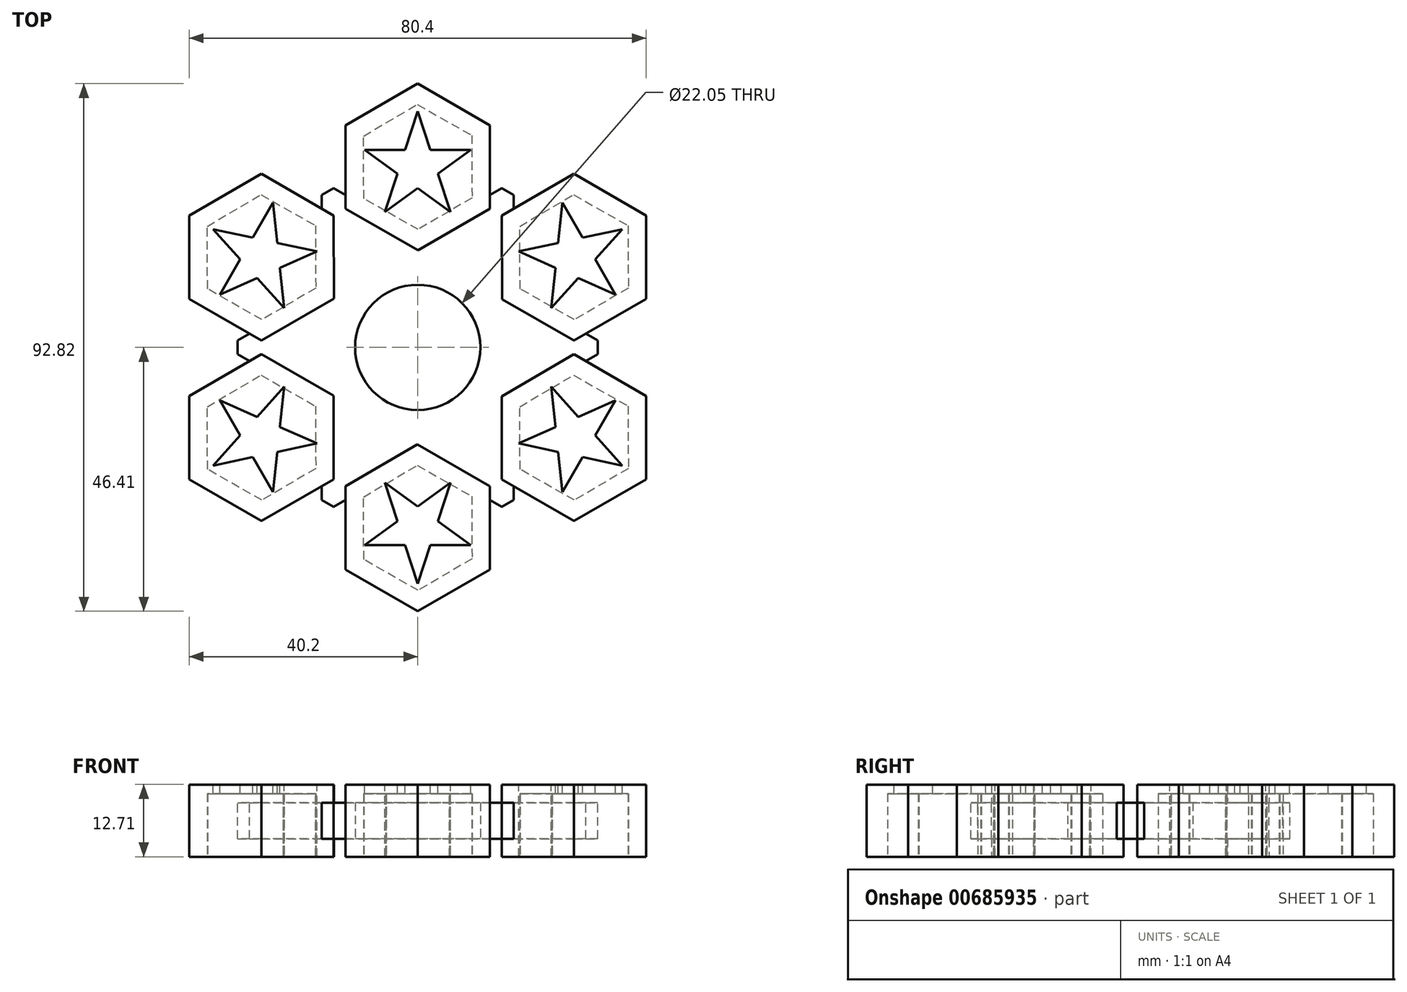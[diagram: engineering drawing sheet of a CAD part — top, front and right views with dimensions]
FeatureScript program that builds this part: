
annotation { "Feature Type Name" : "Feature", "Feature Type Description" : "" }
export const myFeature = defineFeature(function(context is Context, id is Id, definition is map)
    precondition{}
    {
        {
            var Q0;
            Q0=qCreatedBy(makeId("Top.planeOp"),FACE);
            var sketch = newSketch(context, id + "F0", { "sketchPlane" : qUnion([Q0])});
            skCircle(sketch, "E0", {"center": v(0, 0) * mm, "radius": 11.02 * mm});
            skCircle(sketch, "E1", {"center": v(0, 0) * mm, "radius": 15.88 * mm});
            skCircle(sketch, "E2.cCircle", {"center": v(0, 31.75) * mm, "radius": 9.53 * mm, "construction": true});
            skLineSegment(sketch, "E2.0", {"start": v(9.56, 26.3) * mm, "end": v(0.07, 20.75) * mm});
            skLineSegment(sketch, "E2.1", {"start": v(0.07, 20.75) * mm, "end": v(-9.5, 26.2) * mm});
            skLineSegment(sketch, "E2.2", {"start": v(-9.5, 26.2) * mm, "end": v(-9.56, 37.2) * mm});
            skLineSegment(sketch, "E2.3", {"start": v(-9.56, 37.2) * mm, "end": v(-0.07, 42.75) * mm});
            skLineSegment(sketch, "E2.4", {"start": v(-0.07, 42.75) * mm, "end": v(9.5, 37.3) * mm});
            skLineSegment(sketch, "E2.5", {"start": v(9.5, 37.3) * mm, "end": v(9.56, 26.3) * mm});
            skPoint(sketch, "E2.0.midPoint", {"position": v(4.81, 23.53) * mm});
            skLineSegment(sketch, "E3.1.0", {"start": v(-18, 21.43) * mm, "end": v(-17.94, 10.43) * mm});
            skLineSegment(sketch, "E3.1.1", {"start": v(-27.56, 26.87) * mm, "end": v(-18, 21.43) * mm});
            skLineSegment(sketch, "E3.1.2", {"start": v(-37.06, 21.32) * mm, "end": v(-27.56, 26.87) * mm});
            skLineSegment(sketch, "E3.1.3", {"start": v(-36.99, 10.32) * mm, "end": v(-37.06, 21.32) * mm});
            skLineSegment(sketch, "E3.1.4", {"start": v(-27.43, 4.88) * mm, "end": v(-36.99, 10.32) * mm});
            skLineSegment(sketch, "E3.1.5", {"start": v(-17.94, 10.43) * mm, "end": v(-27.43, 4.88) * mm});
            skCircle(sketch, "E3.1.6", {"center": v(-27.5, 15.87) * mm, "radius": 9.53 * mm, "construction": true});
            skPoint(sketch, "E3.1.7", {"position": v(-17.97, 15.93) * mm});
            skLineSegment(sketch, "E3.2.0", {"start": v(-27.56, -4.88) * mm, "end": v(-18, -10.32) * mm});
            skLineSegment(sketch, "E3.2.1", {"start": v(-37.06, -10.43) * mm, "end": v(-27.56, -4.88) * mm});
            skLineSegment(sketch, "E3.2.2", {"start": v(-36.99, -21.43) * mm, "end": v(-37.06, -10.43) * mm});
            skLineSegment(sketch, "E3.2.3", {"start": v(-27.43, -26.87) * mm, "end": v(-36.99, -21.43) * mm});
            skLineSegment(sketch, "E3.2.4", {"start": v(-17.94, -21.32) * mm, "end": v(-27.43, -26.87) * mm});
            skLineSegment(sketch, "E3.2.5", {"start": v(-18, -10.32) * mm, "end": v(-17.94, -21.32) * mm});
            skCircle(sketch, "E3.2.6", {"center": v(-27.5, -15.88) * mm, "radius": 9.53 * mm, "construction": true});
            skPoint(sketch, "E3.2.7", {"position": v(-22.79, -7.6) * mm});
            skLineSegment(sketch, "E4.2.3.0", {"start": v(-9.56, -26.3) * mm, "end": v(-0.07, -20.75) * mm});
            skLineSegment(sketch, "E4.3.3.0", {"start": v(-9.5, -37.3) * mm, "end": v(-9.56, -26.3) * mm});
            skLineSegment(sketch, "E4.6.3.0", {"start": v(0.07, -42.75) * mm, "end": v(-9.5, -37.3) * mm});
            skLineSegment(sketch, "E4.9.3.0", {"start": v(9.56, -37.2) * mm, "end": v(0.07, -42.75) * mm});
            skLineSegment(sketch, "E4.12.3.0", {"start": v(9.5, -26.2) * mm, "end": v(9.56, -37.2) * mm});
            skLineSegment(sketch, "E4.15.3.0", {"start": v(-0.07, -20.75) * mm, "end": v(9.5, -26.2) * mm});
            skCircle(sketch, "E4.18.3.0", {"center": v(0, -31.75) * mm, "radius": 9.53 * mm, "construction": true});
            skPoint(sketch, "E4.20.3.0", {"position": v(-4.81, -23.53) * mm});
            skLineSegment(sketch, "E4.2.4.0", {"start": v(18, -21.43) * mm, "end": v(17.94, -10.43) * mm});
            skLineSegment(sketch, "E4.3.4.0", {"start": v(27.56, -26.87) * mm, "end": v(18, -21.43) * mm});
            skLineSegment(sketch, "E4.6.4.0", {"start": v(37.06, -21.32) * mm, "end": v(27.56, -26.87) * mm});
            skLineSegment(sketch, "E4.9.4.0", {"start": v(36.99, -10.32) * mm, "end": v(37.06, -21.32) * mm});
            skLineSegment(sketch, "E4.12.4.0", {"start": v(27.43, -4.88) * mm, "end": v(36.99, -10.32) * mm});
            skLineSegment(sketch, "E4.15.4.0", {"start": v(17.94, -10.43) * mm, "end": v(27.43, -4.88) * mm});
            skCircle(sketch, "E4.18.4.0", {"center": v(27.5, -15.88) * mm, "radius": 9.53 * mm, "construction": true});
            skPoint(sketch, "E4.20.4.0", {"position": v(17.97, -15.93) * mm});
            skLineSegment(sketch, "E4.2.5.0", {"start": v(27.56, 4.88) * mm, "end": v(18, 10.32) * mm});
            skLineSegment(sketch, "E4.3.5.0", {"start": v(37.06, 10.43) * mm, "end": v(27.56, 4.88) * mm});
            skLineSegment(sketch, "E4.6.5.0", {"start": v(36.99, 21.43) * mm, "end": v(37.06, 10.43) * mm});
            skLineSegment(sketch, "E4.9.5.0", {"start": v(27.43, 26.87) * mm, "end": v(36.99, 21.43) * mm});
            skLineSegment(sketch, "E4.12.5.0", {"start": v(17.94, 21.32) * mm, "end": v(27.43, 26.87) * mm});
            skLineSegment(sketch, "E4.15.5.0", {"start": v(18, 10.32) * mm, "end": v(17.94, 21.32) * mm});
            skCircle(sketch, "E4.18.5.0", {"center": v(27.5, 15.87) * mm, "radius": 9.53 * mm, "construction": true});
            skPoint(sketch, "E4.20.5.0", {"position": v(22.79, 7.6) * mm});
            skCircle(sketch, "E5.cCircle", {"center": v(0, 31.75) * mm, "radius": 12.7 * mm, "construction": true});
            skLineSegment(sketch, "E5.0", {"start": v(12.7, 24.42) * mm, "end": v(0, 17.09) * mm});
            skLineSegment(sketch, "E5.1", {"start": v(0, 17.09) * mm, "end": v(-12.7, 24.42) * mm});
            skLineSegment(sketch, "E5.2", {"start": v(-12.7, 24.42) * mm, "end": v(-12.7, 39.08) * mm});
            skLineSegment(sketch, "E5.3", {"start": v(-12.7, 39.08) * mm, "end": v(0, 46.41) * mm});
            skLineSegment(sketch, "E5.4", {"start": v(0, 46.41) * mm, "end": v(12.7, 39.08) * mm});
            skLineSegment(sketch, "E5.5", {"start": v(12.7, 39.08) * mm, "end": v(12.7, 24.42) * mm});
            skPoint(sketch, "E5.0.midPoint", {"position": v(6.35, 20.75) * mm});
            skCircle(sketch, "E6.1.0", {"center": v(-27.5, 15.87) * mm, "radius": 12.7 * mm, "construction": true});
            skLineSegment(sketch, "E6.1.1", {"start": v(-40.2, 8.54) * mm, "end": v(-40.2, 23.2) * mm});
            skLineSegment(sketch, "E6.1.2", {"start": v(-40.2, 23.2) * mm, "end": v(-27.5, 30.54) * mm});
            skLineSegment(sketch, "E6.1.3", {"start": v(-14.8, 8.54) * mm, "end": v(-27.5, 1.21) * mm});
            skPoint(sketch, "E6.1.7", {"position": v(-14.8, 15.88) * mm});
            skLineSegment(sketch, "E6.1.9", {"start": v(-27.5, 30.54) * mm, "end": v(-14.8, 23.2) * mm});
            skLineSegment(sketch, "E6.1.10", {"start": v(-14.8, 23.2) * mm, "end": v(-14.8, 8.54) * mm});
            skLineSegment(sketch, "E6.1.16", {"start": v(-27.5, 1.21) * mm, "end": v(-40.2, 8.54) * mm});
            skCircle(sketch, "E6.2.0", {"center": v(-27.5, -15.88) * mm, "radius": 12.7 * mm, "construction": true});
            skLineSegment(sketch, "E6.2.1", {"start": v(-27.5, -30.54) * mm, "end": v(-40.2, -23.2) * mm});
            skLineSegment(sketch, "E6.2.2", {"start": v(-40.2, -23.2) * mm, "end": v(-40.2, -8.54) * mm});
            skLineSegment(sketch, "E6.2.3", {"start": v(-14.8, -8.54) * mm, "end": v(-14.8, -23.2) * mm});
            skPoint(sketch, "E6.2.7", {"position": v(-21.15, -4.88) * mm});
            skLineSegment(sketch, "E6.2.9", {"start": v(-40.2, -8.54) * mm, "end": v(-27.5, -1.21) * mm});
            skLineSegment(sketch, "E6.2.10", {"start": v(-27.5, -1.21) * mm, "end": v(-14.8, -8.54) * mm});
            skLineSegment(sketch, "E6.2.16", {"start": v(-14.8, -23.2) * mm, "end": v(-27.5, -30.54) * mm});
            skCircle(sketch, "E6.3.0", {"center": v(0, -31.75) * mm, "radius": 12.7 * mm, "construction": true});
            skLineSegment(sketch, "E6.3.1", {"start": v(12.7, -39.08) * mm, "end": v(0, -46.41) * mm});
            skLineSegment(sketch, "E6.3.2", {"start": v(0, -46.41) * mm, "end": v(-12.7, -39.08) * mm});
            skLineSegment(sketch, "E6.3.3", {"start": v(0, -17.09) * mm, "end": v(12.7, -24.42) * mm});
            skPoint(sketch, "E6.3.7", {"position": v(-6.35, -20.75) * mm});
            skLineSegment(sketch, "E6.3.9", {"start": v(-12.7, -39.08) * mm, "end": v(-12.7, -24.42) * mm});
            skLineSegment(sketch, "E6.3.10", {"start": v(-12.7, -24.42) * mm, "end": v(0, -17.09) * mm});
            skLineSegment(sketch, "E6.3.16", {"start": v(12.7, -24.42) * mm, "end": v(12.7, -39.08) * mm});
            skCircle(sketch, "E6.4.0", {"center": v(27.5, -15.87) * mm, "radius": 12.7 * mm, "construction": true});
            skLineSegment(sketch, "E6.4.1", {"start": v(40.2, -8.54) * mm, "end": v(40.2, -23.2) * mm});
            skLineSegment(sketch, "E6.4.2", {"start": v(40.2, -23.2) * mm, "end": v(27.5, -30.54) * mm});
            skLineSegment(sketch, "E6.4.3", {"start": v(14.8, -8.54) * mm, "end": v(27.5, -1.21) * mm});
            skPoint(sketch, "E6.4.7", {"position": v(14.8, -15.88) * mm});
            skCircle(sketch, "E6.4.8", {"center": v(27.5, -15.87) * mm, "radius": 9.53 * mm, "construction": true});
            skLineSegment(sketch, "E6.4.9", {"start": v(27.5, -30.54) * mm, "end": v(14.8, -23.2) * mm});
            skLineSegment(sketch, "E6.4.10", {"start": v(14.8, -23.2) * mm, "end": v(14.8, -8.54) * mm});
            skLineSegment(sketch, "E6.4.16", {"start": v(27.5, -1.21) * mm, "end": v(40.2, -8.54) * mm});
            skCircle(sketch, "E6.5.0", {"center": v(27.5, 15.88) * mm, "radius": 12.7 * mm, "construction": true});
            skLineSegment(sketch, "E6.5.1", {"start": v(27.5, 30.54) * mm, "end": v(40.2, 23.2) * mm});
            skLineSegment(sketch, "E6.5.2", {"start": v(40.2, 23.2) * mm, "end": v(40.2, 8.54) * mm});
            skLineSegment(sketch, "E6.5.3", {"start": v(14.8, 8.54) * mm, "end": v(14.8, 23.2) * mm});
            skPoint(sketch, "E6.5.7", {"position": v(21.15, 4.88) * mm});
            skCircle(sketch, "E6.5.8", {"center": v(27.5, 15.88) * mm, "radius": 9.53 * mm, "construction": true});
            skLineSegment(sketch, "E6.5.9", {"start": v(40.2, 8.54) * mm, "end": v(27.5, 1.21) * mm});
            skLineSegment(sketch, "E6.5.10", {"start": v(27.5, 1.21) * mm, "end": v(14.8, 8.54) * mm});
            skLineSegment(sketch, "E6.5.16", {"start": v(14.8, 23.2) * mm, "end": v(27.5, 30.54) * mm});
            skLineSegment(sketch, "E7", {"start": v(-14.8, 23.2) * mm, "end": v(-12.7, 24.42) * mm});
            skLineSegment(sketch, "E8", {"start": v(12.7, 24.42) * mm, "end": v(14.8, 23.2) * mm});
            skLineSegment(sketch, "E9", {"start": v(27.5, 1.21) * mm, "end": v(27.5, -1.21) * mm});
            skLineSegment(sketch, "E10", {"start": v(12.7, -24.42) * mm, "end": v(14.8, -23.2) * mm});
            skLineSegment(sketch, "E11", {"start": v(-14.8, -23.2) * mm, "end": v(-12.7, -24.42) * mm});
            skLineSegment(sketch, "E12", {"start": v(-27.5, 1.21) * mm, "end": v(-27.5, -1.21) * mm});
            skSolve(sketch);
        }
        {
            var Q0;
            Q0=makeQuery(id+"F0.imprint","IMPRINT",FACE,{"disambiguationData":[TD([[makeQuery(id+"F0.imprint","IMPRINT",EDGE,{"derivedFrom":sQuery(id+"F0.wireOp",EDGE,"E2.0")}),1.0]])]});
            var Q1;
            Q1=makeQuery(id+"F0.imprint","IMPRINT",FACE,{"disambiguationData":[TD([[makeQuery(id+"F0.imprint","IMPRINT",EDGE,{"derivedFrom":sQuery(id+"F0.wireOp",EDGE,"E1")}),-1.0]])]});
            var Q2;
            Q2=makeQuery(id+"F0.imprint","IMPRINT",FACE,{"disambiguationData":[TD([[makeQuery(id+"F0.imprint","IMPRINT",EDGE,{"derivedFrom":sQuery(id+"F0.wireOp",EDGE,"E6.1.1")}),-1.0]])]});
            var Q3;
            Q3=makeQuery(id+"F0.imprint","IMPRINT",FACE,{"disambiguationData":[TD([[makeQuery(id+"F0.imprint","IMPRINT",EDGE,{"derivedFrom":sQuery(id+"F0.wireOp",EDGE,"E6.2.1")}),-1.0]])]});
            var Q4;
            Q4=makeQuery(id+"F0.imprint","IMPRINT",FACE,{"disambiguationData":[TD([[makeQuery(id+"F0.imprint","IMPRINT",EDGE,{"derivedFrom":sQuery(id+"F0.wireOp",EDGE,"E6.3.1")}),-1.0]])]});
            var Q5;
            Q5=makeQuery(id+"F0.imprint","IMPRINT",FACE,{"disambiguationData":[TD([[makeQuery(id+"F0.imprint","IMPRINT",EDGE,{"derivedFrom":sQuery(id+"F0.wireOp",EDGE,"E6.4.1")}),-1.0]])]});
            var Q6;
            Q6=makeQuery(id+"F0.imprint","IMPRINT",FACE,{"disambiguationData":[TD([[makeQuery(id+"F0.imprint","IMPRINT",EDGE,{"derivedFrom":sQuery(id+"F0.wireOp",EDGE,"E6.5.1")}),-1.0]])]});
            var Q7;
            Q7=makeQuery(id+"F0.imprint","IMPRINT",FACE,{"disambiguationData":[TD([[makeQuery(id+"F0.imprint","IMPRINT",EDGE,{"derivedFrom":sQuery(id+"F0.wireOp",EDGE,"E0")}),-1.0]])]});
            extrude(context, id + "F1", {"entities" : qUnion([Q0, Q1, Q2, Q3, Q4, Q5, Q6, Q7]), "depth" : 6.35 * mm, "offsetDistance" : 25.4 * mm});
        }
        {
            var Q0;
            Q0=makeQuery(id+"F1.opExtrude","CAP_FACE",FACE,{"disambiguationData":[OSD([sQuery(id+"F0.wireOp",EDGE,"E1"),sQuery(id+"F0.wireOp",EDGE,"E2.0"),sQuery(id+"F0.wireOp",EDGE,"E2.1"),sQuery(id+"F0.wireOp",EDGE,"E2.2"),sQuery(id+"F0.wireOp",EDGE,"E2.3"),sQuery(id+"F0.wireOp",EDGE,"E2.4"),sQuery(id+"F0.wireOp",EDGE,"E5.2"),sQuery(id+"F0.wireOp",EDGE,"E5.3"),sQuery(id+"F0.wireOp",EDGE,"E5.4"),sQuery(id+"F0.wireOp",EDGE,"E5.5"),sQuery(id+"F0.wireOp",EDGE,"E6.1.1"),sQuery(id+"F0.wireOp",EDGE,"E6.1.2"),sQuery(id+"F0.wireOp",EDGE,"E3.1.1"),sQuery(id+"F0.wireOp",EDGE,"E6.1.9"),sQuery(id+"F0.wireOp",EDGE,"E3.1.2"),sQuery(id+"F0.wireOp",EDGE,"E3.1.3"),sQuery(id+"F0.wireOp",EDGE,"E3.1.4"),sQuery(id+"F0.wireOp",EDGE,"E3.1.5"),sQuery(id+"F0.wireOp",EDGE,"E3.1.0"),sQuery(id+"F0.wireOp",EDGE,"E6.1.16"),sQuery(id+"F0.wireOp",EDGE,"E6.2.1"),sQuery(id+"F0.wireOp",EDGE,"E6.2.2"),sQuery(id+"F0.wireOp",EDGE,"E3.2.1"),sQuery(id+"F0.wireOp",EDGE,"E6.2.9"),sQuery(id+"F0.wireOp",EDGE,"E3.2.2"),sQuery(id+"F0.wireOp",EDGE,"E3.2.3"),sQuery(id+"F0.wireOp",EDGE,"E3.2.4"),sQuery(id+"F0.wireOp",EDGE,"E3.2.5"),sQuery(id+"F0.wireOp",EDGE,"E3.2.0"),sQuery(id+"F0.wireOp",EDGE,"E6.2.16"),sQuery(id+"F0.wireOp",EDGE,"E6.3.1"),sQuery(id+"F0.wireOp",EDGE,"E6.3.2"),sQuery(id+"F0.wireOp",EDGE,"E4.3.3.0"),sQuery(id+"F0.wireOp",EDGE,"E6.3.9"),sQuery(id+"F0.wireOp",EDGE,"E4.6.3.0"),sQuery(id+"F0.wireOp",EDGE,"E4.9.3.0"),sQuery(id+"F0.wireOp",EDGE,"E4.12.3.0"),sQuery(id+"F0.wireOp",EDGE,"E4.15.3.0"),sQuery(id+"F0.wireOp",EDGE,"E4.2.3.0"),sQuery(id+"F0.wireOp",EDGE,"E6.3.16"),sQuery(id+"F0.wireOp",EDGE,"E6.4.1"),sQuery(id+"F0.wireOp",EDGE,"E6.4.2"),sQuery(id+"F0.wireOp",EDGE,"E4.3.4.0"),sQuery(id+"F0.wireOp",EDGE,"E6.4.9"),sQuery(id+"F0.wireOp",EDGE,"E4.6.4.0"),sQuery(id+"F0.wireOp",EDGE,"E4.9.4.0"),sQuery(id+"F0.wireOp",EDGE,"E4.12.4.0"),sQuery(id+"F0.wireOp",EDGE,"E4.15.4.0"),sQuery(id+"F0.wireOp",EDGE,"E4.2.4.0"),sQuery(id+"F0.wireOp",EDGE,"E6.4.16"),sQuery(id+"F0.wireOp",EDGE,"E6.5.1"),sQuery(id+"F0.wireOp",EDGE,"E6.5.2"),sQuery(id+"F0.wireOp",EDGE,"E2.5"),sQuery(id+"F0.wireOp",EDGE,"E4.3.5.0"),sQuery(id+"F0.wireOp",EDGE,"E6.5.9"),sQuery(id+"F0.wireOp",EDGE,"E4.6.5.0"),sQuery(id+"F0.wireOp",EDGE,"E4.9.5.0"),sQuery(id+"F0.wireOp",EDGE,"E4.12.5.0"),sQuery(id+"F0.wireOp",EDGE,"E4.15.5.0"),sQuery(id+"F0.wireOp",EDGE,"E4.2.5.0"),sQuery(id+"F0.wireOp",EDGE,"E6.5.16"),sQuery(id+"F0.wireOp",EDGE,"E7"),sQuery(id+"F0.wireOp",EDGE,"E8"),sQuery(id+"F0.wireOp",EDGE,"E9"),sQuery(id+"F0.wireOp",EDGE,"E10"),sQuery(id+"F0.wireOp",EDGE,"E11"),sQuery(id+"F0.wireOp",EDGE,"E12")])],"isStart":false});
            var sketch = newSketch(context, id + "F2", { "sketchPlane" : qUnion([Q0])});
            skLineSegment(sketch, "E13.0", {"start": v(0, 46.41) * mm, "end": v(12.7, 39.08) * mm});
            skPoint(sketch, "E14.0", {"position": v(-6.35, 42.75) * mm});
            skLineSegment(sketch, "E15.0", {"start": v(-12.7, 39.08) * mm, "end": v(0, 46.41) * mm});
            skLineSegment(sketch, "E16.0", {"start": v(-12.7, 24.42) * mm, "end": v(-12.7, 39.08) * mm});
            skLineSegment(sketch, "E17.0", {"start": v(12.7, 39.08) * mm, "end": v(12.7, 24.42) * mm});
            skLineSegment(sketch, "E18", {"start": v(-12.7, 24.42) * mm, "end": v(0.07, 17.08) * mm});
            skLineSegment(sketch, "E19", {"start": v(0.07, 17.08) * mm, "end": v(12.7, 24.42) * mm});
            skLineSegment(sketch, "E20.0", {"start": v(-9.56, 37.2) * mm, "end": v(-0.07, 42.75) * mm});
            skLineSegment(sketch, "E21.0", {"start": v(-9.5, 26.2) * mm, "end": v(-9.56, 37.2) * mm});
            skLineSegment(sketch, "E22.0", {"start": v(0.07, 20.75) * mm, "end": v(-9.5, 26.2) * mm});
            skLineSegment(sketch, "E23.0", {"start": v(9.56, 26.3) * mm, "end": v(0.07, 20.75) * mm});
            skLineSegment(sketch, "E24.0", {"start": v(9.5, 37.3) * mm, "end": v(9.56, 26.3) * mm});
            skLineSegment(sketch, "E25.0", {"start": v(-0.07, 42.75) * mm, "end": v(9.5, 37.3) * mm});
            skLineSegment(sketch, "E26.1.0", {"start": v(-40.2, 8.54) * mm, "end": v(-40.2, 23.2) * mm});
            skLineSegment(sketch, "E26.1.1", {"start": v(-27.5, 1.21) * mm, "end": v(-40.2, 8.54) * mm});
            skLineSegment(sketch, "E26.1.2", {"start": v(-27.5, 1.21) * mm, "end": v(-14.76, 8.6) * mm});
            skLineSegment(sketch, "E26.1.3", {"start": v(-14.76, 8.6) * mm, "end": v(-14.8, 23.2) * mm});
            skLineSegment(sketch, "E26.1.4", {"start": v(-27.5, 30.54) * mm, "end": v(-14.8, 23.2) * mm});
            skLineSegment(sketch, "E26.1.5", {"start": v(-40.2, 23.2) * mm, "end": v(-27.5, 30.54) * mm});
            skLineSegment(sketch, "E26.1.6", {"start": v(-37.06, 21.32) * mm, "end": v(-27.56, 26.87) * mm});
            skLineSegment(sketch, "E26.1.7", {"start": v(-36.99, 10.32) * mm, "end": v(-37.06, 21.32) * mm});
            skLineSegment(sketch, "E26.1.8", {"start": v(-27.43, 4.88) * mm, "end": v(-36.99, 10.32) * mm});
            skLineSegment(sketch, "E26.1.9", {"start": v(-17.94, 10.43) * mm, "end": v(-27.43, 4.88) * mm});
            skLineSegment(sketch, "E26.1.10", {"start": v(-18, 21.43) * mm, "end": v(-17.94, 10.43) * mm});
            skLineSegment(sketch, "E26.1.11", {"start": v(-27.56, 26.87) * mm, "end": v(-18, 21.43) * mm});
            skLineSegment(sketch, "E26.2.0", {"start": v(-27.5, -30.54) * mm, "end": v(-40.2, -23.2) * mm});
            skLineSegment(sketch, "E26.2.1", {"start": v(-14.8, -23.2) * mm, "end": v(-27.5, -30.54) * mm});
            skLineSegment(sketch, "E26.2.2", {"start": v(-14.8, -23.2) * mm, "end": v(-14.83, -8.48) * mm});
            skLineSegment(sketch, "E26.2.3", {"start": v(-14.83, -8.48) * mm, "end": v(-27.5, -1.21) * mm});
            skLineSegment(sketch, "E26.2.4", {"start": v(-40.2, -8.54) * mm, "end": v(-27.5, -1.21) * mm});
            skLineSegment(sketch, "E26.2.5", {"start": v(-40.2, -23.2) * mm, "end": v(-40.2, -8.54) * mm});
            skLineSegment(sketch, "E26.2.6", {"start": v(-36.99, -21.43) * mm, "end": v(-37.06, -10.43) * mm});
            skLineSegment(sketch, "E26.2.7", {"start": v(-27.43, -26.87) * mm, "end": v(-36.99, -21.43) * mm});
            skLineSegment(sketch, "E26.2.8", {"start": v(-17.94, -21.32) * mm, "end": v(-27.43, -26.87) * mm});
            skLineSegment(sketch, "E26.2.9", {"start": v(-18, -10.32) * mm, "end": v(-17.94, -21.32) * mm});
            skLineSegment(sketch, "E26.2.10", {"start": v(-27.56, -4.88) * mm, "end": v(-18, -10.32) * mm});
            skLineSegment(sketch, "E26.2.11", {"start": v(-37.06, -10.43) * mm, "end": v(-27.56, -4.88) * mm});
            skPoint(sketch, "E26.center", {"position": v(0, 0) * mm});
            skLineSegment(sketch, "E27.1.3.0", {"start": v(12.7, -39.08) * mm, "end": v(0, -46.41) * mm});
            skLineSegment(sketch, "E27.3.3.0", {"start": v(12.7, -24.42) * mm, "end": v(12.7, -39.08) * mm});
            skLineSegment(sketch, "E27.6.3.0", {"start": v(12.7, -24.42) * mm, "end": v(-0.07, -17.08) * mm});
            skLineSegment(sketch, "E27.9.3.0", {"start": v(-0.07, -17.08) * mm, "end": v(-12.7, -24.42) * mm});
            skLineSegment(sketch, "E27.12.3.0", {"start": v(-12.7, -39.08) * mm, "end": v(-12.7, -24.42) * mm});
            skLineSegment(sketch, "E27.15.3.0", {"start": v(0, -46.41) * mm, "end": v(-12.7, -39.08) * mm});
            skLineSegment(sketch, "E27.18.3.0", {"start": v(0.07, -42.75) * mm, "end": v(-9.5, -37.3) * mm});
            skLineSegment(sketch, "E27.21.3.0", {"start": v(9.56, -37.2) * mm, "end": v(0.07, -42.75) * mm});
            skLineSegment(sketch, "E27.24.3.0", {"start": v(9.5, -26.2) * mm, "end": v(9.56, -37.2) * mm});
            skLineSegment(sketch, "E27.27.3.0", {"start": v(-0.07, -20.75) * mm, "end": v(9.5, -26.2) * mm});
            skLineSegment(sketch, "E27.30.3.0", {"start": v(-9.56, -26.3) * mm, "end": v(-0.07, -20.75) * mm});
            skLineSegment(sketch, "E27.33.3.0", {"start": v(-9.5, -37.3) * mm, "end": v(-9.56, -26.3) * mm});
            skLineSegment(sketch, "E27.1.4.0", {"start": v(40.2, -8.54) * mm, "end": v(40.2, -23.2) * mm});
            skLineSegment(sketch, "E27.3.4.0", {"start": v(27.5, -1.21) * mm, "end": v(40.2, -8.54) * mm});
            skLineSegment(sketch, "E27.6.4.0", {"start": v(27.5, -1.21) * mm, "end": v(14.76, -8.6) * mm});
            skLineSegment(sketch, "E27.9.4.0", {"start": v(14.76, -8.6) * mm, "end": v(14.8, -23.2) * mm});
            skLineSegment(sketch, "E27.12.4.0", {"start": v(27.5, -30.54) * mm, "end": v(14.8, -23.2) * mm});
            skLineSegment(sketch, "E27.15.4.0", {"start": v(40.2, -23.2) * mm, "end": v(27.5, -30.54) * mm});
            skLineSegment(sketch, "E27.18.4.0", {"start": v(37.06, -21.32) * mm, "end": v(27.56, -26.87) * mm});
            skLineSegment(sketch, "E27.21.4.0", {"start": v(36.99, -10.32) * mm, "end": v(37.06, -21.32) * mm});
            skLineSegment(sketch, "E27.24.4.0", {"start": v(27.43, -4.88) * mm, "end": v(36.99, -10.32) * mm});
            skLineSegment(sketch, "E27.27.4.0", {"start": v(17.94, -10.43) * mm, "end": v(27.43, -4.88) * mm});
            skLineSegment(sketch, "E27.30.4.0", {"start": v(18, -21.43) * mm, "end": v(17.94, -10.43) * mm});
            skLineSegment(sketch, "E27.33.4.0", {"start": v(27.56, -26.87) * mm, "end": v(18, -21.43) * mm});
            skLineSegment(sketch, "E27.1.5.0", {"start": v(27.5, 30.54) * mm, "end": v(40.2, 23.2) * mm});
            skLineSegment(sketch, "E27.3.5.0", {"start": v(14.8, 23.2) * mm, "end": v(27.5, 30.54) * mm});
            skLineSegment(sketch, "E27.6.5.0", {"start": v(14.8, 23.2) * mm, "end": v(14.83, 8.48) * mm});
            skLineSegment(sketch, "E27.9.5.0", {"start": v(14.83, 8.48) * mm, "end": v(27.5, 1.21) * mm});
            skLineSegment(sketch, "E27.12.5.0", {"start": v(40.2, 8.54) * mm, "end": v(27.5, 1.21) * mm});
            skLineSegment(sketch, "E27.15.5.0", {"start": v(40.2, 23.2) * mm, "end": v(40.2, 8.54) * mm});
            skLineSegment(sketch, "E27.18.5.0", {"start": v(36.99, 21.43) * mm, "end": v(37.06, 10.43) * mm});
            skLineSegment(sketch, "E27.21.5.0", {"start": v(27.43, 26.87) * mm, "end": v(36.99, 21.43) * mm});
            skLineSegment(sketch, "E27.24.5.0", {"start": v(17.94, 21.32) * mm, "end": v(27.43, 26.87) * mm});
            skLineSegment(sketch, "E27.27.5.0", {"start": v(18, 10.32) * mm, "end": v(17.94, 21.32) * mm});
            skLineSegment(sketch, "E27.30.5.0", {"start": v(27.56, 4.88) * mm, "end": v(18, 10.32) * mm});
            skLineSegment(sketch, "E27.33.5.0", {"start": v(37.06, 10.43) * mm, "end": v(27.56, 4.88) * mm});
            skSolve(sketch);
        }
        {
            var Q0;
            Q0=makeQuery(id+"F2.imprint","IMPRINT",FACE,{"disambiguationData":[TD([[makeQuery(id+"F2.imprint","IMPRINT",EDGE,{"derivedFrom":sQuery(id+"F2.wireOp",EDGE,"E13.0")}),-1.0]])]});
            var Q1;
            Q1=makeQuery(id+"F2.imprint","IMPRINT",FACE,{"disambiguationData":[TD([[makeQuery(id+"F2.imprint","IMPRINT",EDGE,{"derivedFrom":sQuery(id+"F2.wireOp",EDGE,"E27.1.5.0")}),-1.0]])]});
            var Q2;
            Q2=makeQuery(id+"F2.imprint","IMPRINT",FACE,{"disambiguationData":[TD([[makeQuery(id+"F2.imprint","IMPRINT",EDGE,{"derivedFrom":sQuery(id+"F2.wireOp",EDGE,"E27.1.4.0")}),-1.0]])]});
            var Q3;
            Q3=makeQuery(id+"F2.imprint","IMPRINT",FACE,{"disambiguationData":[TD([[makeQuery(id+"F2.imprint","IMPRINT",EDGE,{"derivedFrom":sQuery(id+"F2.wireOp",EDGE,"E27.1.3.0")}),-1.0]])]});
            var Q4;
            Q4=makeQuery(id+"F2.imprint","IMPRINT",FACE,{"disambiguationData":[TD([[makeQuery(id+"F2.imprint","IMPRINT",EDGE,{"derivedFrom":sQuery(id+"F2.wireOp",EDGE,"E26.2.0")}),-1.0]])]});
            var Q5;
            Q5=makeQuery(id+"F2.imprint","IMPRINT",FACE,{"disambiguationData":[TD([[makeQuery(id+"F2.imprint","IMPRINT",EDGE,{"derivedFrom":sQuery(id+"F2.wireOp",EDGE,"E26.1.0")}),-1.0]])]});
            extrude(context, id + "F3", {"entities" : qUnion([Q0, Q1, Q2, Q3, Q4, Q5]), "operationType" : NewBodyOperationType.ADD, "depth" : 1.59 * mm, "offsetDistance" : 25.4 * mm, "hasSecondDirection" : true, "secondDirectionOppositeDirection" : true, "secondDirectionDepth" : 9.52 * mm});
        }
        {
            var Q0;
            Q0=makeQuery(id+"F3.opExtrude","CAP_FACE",FACE,{"disambiguationData":[OSD([sQuery(id+"F2.wireOp",EDGE,"E13.0"),sQuery(id+"F2.wireOp",EDGE,"E15.0"),sQuery(id+"F2.wireOp",EDGE,"E16.0"),sQuery(id+"F2.wireOp",EDGE,"E17.0"),sQuery(id+"F2.wireOp",EDGE,"E18"),sQuery(id+"F2.wireOp",EDGE,"E19"),sQuery(id+"F2.wireOp",EDGE,"E20.0"),sQuery(id+"F2.wireOp",EDGE,"E21.0"),sQuery(id+"F2.wireOp",EDGE,"E22.0"),sQuery(id+"F2.wireOp",EDGE,"E23.0"),sQuery(id+"F2.wireOp",EDGE,"E24.0"),sQuery(id+"F2.wireOp",EDGE,"E25.0")])],"isStart":false});
            var sketch = newSketch(context, id + "F4", { "sketchPlane" : qUnion([Q0])});
            skLineSegment(sketch, "E28.0", {"start": v(-12.7, 39.08) * mm, "end": v(0, 46.41) * mm});
            skLineSegment(sketch, "E29.0", {"start": v(-12.7, 24.42) * mm, "end": v(-12.7, 39.08) * mm});
            skLineSegment(sketch, "E30.0", {"start": v(-12.7, 24.42) * mm, "end": v(0.07, 17.08) * mm});
            skLineSegment(sketch, "E31.0", {"start": v(0.07, 17.08) * mm, "end": v(12.7, 24.42) * mm});
            skLineSegment(sketch, "E32.0", {"start": v(12.7, 39.08) * mm, "end": v(12.7, 24.42) * mm});
            skLineSegment(sketch, "E33.0", {"start": v(0, 46.41) * mm, "end": v(12.7, 39.08) * mm});
            skLineSegment(sketch, "E34.0", {"start": v(14.8, 23.2) * mm, "end": v(27.5, 30.54) * mm});
            skLineSegment(sketch, "E35.0", {"start": v(27.5, 30.54) * mm, "end": v(40.2, 23.2) * mm});
            skLineSegment(sketch, "E36.0", {"start": v(40.2, 23.2) * mm, "end": v(40.2, 8.54) * mm});
            skLineSegment(sketch, "E37.0", {"start": v(40.2, 8.54) * mm, "end": v(27.5, 1.21) * mm});
            skLineSegment(sketch, "E38.0", {"start": v(14.83, 8.48) * mm, "end": v(27.5, 1.21) * mm});
            skLineSegment(sketch, "E39.0", {"start": v(14.8, 23.2) * mm, "end": v(14.83, 8.48) * mm});
            skLineSegment(sketch, "E40.0", {"start": v(27.5, -1.21) * mm, "end": v(14.76, -8.6) * mm});
            skLineSegment(sketch, "E41.0", {"start": v(27.5, -1.21) * mm, "end": v(40.2, -8.54) * mm});
            skLineSegment(sketch, "E42.0", {"start": v(40.2, -8.54) * mm, "end": v(40.2, -23.2) * mm});
            skLineSegment(sketch, "E43.0", {"start": v(40.2, -23.2) * mm, "end": v(27.5, -30.54) * mm});
            skLineSegment(sketch, "E44.0", {"start": v(27.5, -30.54) * mm, "end": v(14.8, -23.2) * mm});
            skLineSegment(sketch, "E45.0", {"start": v(14.76, -8.6) * mm, "end": v(14.8, -23.2) * mm});
            skLineSegment(sketch, "E46.0", {"start": v(12.7, -24.42) * mm, "end": v(-0.07, -17.08) * mm});
            skLineSegment(sketch, "E47.0", {"start": v(12.7, -24.42) * mm, "end": v(12.7, -39.08) * mm});
            skLineSegment(sketch, "E48.0", {"start": v(12.7, -39.08) * mm, "end": v(0, -46.41) * mm});
            skLineSegment(sketch, "E49.0", {"start": v(0, -46.41) * mm, "end": v(-12.7, -39.08) * mm});
            skLineSegment(sketch, "E50.0", {"start": v(-12.7, -39.08) * mm, "end": v(-12.7, -24.42) * mm});
            skLineSegment(sketch, "E51.0", {"start": v(-0.07, -17.08) * mm, "end": v(-12.7, -24.42) * mm});
            skLineSegment(sketch, "E52.0", {"start": v(-14.8, -23.2) * mm, "end": v(-14.83, -8.48) * mm});
            skLineSegment(sketch, "E53.0", {"start": v(-14.8, -23.2) * mm, "end": v(-27.5, -30.54) * mm});
            skLineSegment(sketch, "E54.0", {"start": v(-27.5, -30.54) * mm, "end": v(-40.2, -23.2) * mm});
            skLineSegment(sketch, "E55.0", {"start": v(-40.2, -23.2) * mm, "end": v(-40.2, -8.54) * mm});
            skLineSegment(sketch, "E56.0", {"start": v(-40.2, -8.54) * mm, "end": v(-27.5, -1.21) * mm});
            skLineSegment(sketch, "E57.0", {"start": v(-14.83, -8.48) * mm, "end": v(-27.5, -1.21) * mm});
            skLineSegment(sketch, "E58.0", {"start": v(-27.5, 1.21) * mm, "end": v(-14.76, 8.6) * mm});
            skLineSegment(sketch, "E59.0", {"start": v(-27.5, 1.21) * mm, "end": v(-40.2, 8.54) * mm});
            skLineSegment(sketch, "E60.0", {"start": v(-40.2, 8.54) * mm, "end": v(-40.2, 23.2) * mm});
            skLineSegment(sketch, "E61.0", {"start": v(-40.2, 23.2) * mm, "end": v(-27.5, 30.54) * mm});
            skLineSegment(sketch, "E62.0", {"start": v(-27.5, 30.54) * mm, "end": v(-14.8, 23.2) * mm});
            skLineSegment(sketch, "E63.0", {"start": v(-14.76, 8.6) * mm, "end": v(-14.8, 23.2) * mm});
            skSolve(sketch);
        }
        {
            var Q0;
            Q0=makeQuery(id+"F4.imprint","IMPRINT",FACE,{"disambiguationData":[TD([[makeQuery(id+"F4.imprint","IMPRINT",EDGE,{"derivedFrom":sQuery(id+"F4.wireOp",EDGE,"E28.0")}),-1.0]])]});
            var Q1;
            Q1=makeQuery(id+"F4.imprint","IMPRINT",FACE,{"disambiguationData":[TD([[makeQuery(id+"F4.imprint","IMPRINT",EDGE,{"derivedFrom":makeQuery(id+"F3.opExtrude","CAP_EDGE",EDGE,{"disambiguationData":[OSD([sQuery(id+"F2.wireOp",EDGE,"E20.0")])],"isStart":false})}),-1.0]])]});
            var Q2;
            Q2=makeQuery(id+"F4.imprint","IMPRINT",FACE,{"disambiguationData":[TD([[makeQuery(id+"F4.imprint","IMPRINT",EDGE,{"derivedFrom":sQuery(id+"F4.wireOp",EDGE,"E34.0")}),-1.0]])]});
            var Q3;
            Q3=makeQuery(id+"F4.imprint","IMPRINT",FACE,{"disambiguationData":[TD([[makeQuery(id+"F4.imprint","IMPRINT",EDGE,{"derivedFrom":sQuery(id+"F4.wireOp",EDGE,"E40.0")}),1.0]])]});
            var Q4;
            Q4=makeQuery(id+"F4.imprint","IMPRINT",FACE,{"disambiguationData":[TD([[makeQuery(id+"F4.imprint","IMPRINT",EDGE,{"derivedFrom":sQuery(id+"F4.wireOp",EDGE,"E46.0")}),1.0]])]});
            var Q5;
            Q5=makeQuery(id+"F4.imprint","IMPRINT",FACE,{"disambiguationData":[TD([[makeQuery(id+"F4.imprint","IMPRINT",EDGE,{"derivedFrom":sQuery(id+"F4.wireOp",EDGE,"E52.0")}),1.0]])]});
            var Q6;
            Q6=makeQuery(id+"F4.imprint","IMPRINT",FACE,{"disambiguationData":[TD([[makeQuery(id+"F4.imprint","IMPRINT",EDGE,{"derivedFrom":sQuery(id+"F4.wireOp",EDGE,"E58.0")}),1.0]])]});
            extrude(context, id + "F5", {"entities" : qUnion([Q0, Q1, Q2, Q3, Q4, Q5, Q6]), "operationType" : NewBodyOperationType.ADD, "depth" : 1.59 * mm, "offsetDistance" : 25.4 * mm});
        }
        {
            var Q0;
            Q0=makeQuery(id+"F5.opExtrude","CAP_FACE",FACE,{"disambiguationData":[OSD([sQuery(id+"F4.wireOp",EDGE,"E28.0"),sQuery(id+"F4.wireOp",EDGE,"E29.0"),sQuery(id+"F4.wireOp",EDGE,"E30.0"),sQuery(id+"F4.wireOp",EDGE,"E31.0"),sQuery(id+"F4.wireOp",EDGE,"E32.0"),sQuery(id+"F4.wireOp",EDGE,"E33.0")])],"isStart":false});
            var sketch = newSketch(context, id + "F6", { "sketchPlane" : qUnion([Q0])});
            skCircle(sketch, "E64.cCircle", {"center": v(0, 31.75) * mm, "radius": 7.94 * mm, "construction": true});
            skPoint(sketch, "E64.cCircle.centerSnap0", {"position": v(-12.7, 31.75) * mm});
            skLineSegment(sketch, "E64.0", {"start": v(5.77, 23.81) * mm, "end": v(-5.77, 23.81) * mm});
            skLineSegment(sketch, "E64.1", {"start": v(-5.77, 23.81) * mm, "end": v(-9.33, 34.78) * mm});
            skLineSegment(sketch, "E64.2", {"start": v(-9.33, 34.78) * mm, "end": v(0, 41.56) * mm});
            skLineSegment(sketch, "E64.3", {"start": v(0, 41.56) * mm, "end": v(9.33, 34.78) * mm});
            skLineSegment(sketch, "E64.4", {"start": v(9.33, 34.78) * mm, "end": v(5.77, 23.81) * mm});
            skPoint(sketch, "E64.0.midPoint", {"position": v(0, 23.81) * mm});
            skLineSegment(sketch, "E65", {"start": v(-5.77, 23.81) * mm, "end": v(-3.56, 30.6) * mm});
            skLineSegment(sketch, "E66", {"start": v(0, 41.56) * mm, "end": v(2.2, 34.78) * mm});
            skLineSegment(sketch, "E67", {"start": v(5.77, 23.81) * mm, "end": v(0, 28) * mm});
            skLineSegment(sketch, "E68", {"start": v(-9.33, 34.78) * mm, "end": v(-2.2, 34.78) * mm});
            skLineSegment(sketch, "E69", {"start": v(9.33, 34.78) * mm, "end": v(3.56, 30.6) * mm});
            skLineSegment(sketch, "E70.trimOffspring", {"start": v(2.2, 34.78) * mm, "end": v(9.33, 34.78) * mm});
            skLineSegment(sketch, "E71.trimOffspring", {"start": v(-2.2, 34.78) * mm, "end": v(0, 41.56) * mm});
            skLineSegment(sketch, "E72.trimOffspring", {"start": v(-3.56, 30.6) * mm, "end": v(-9.33, 34.78) * mm});
            skLineSegment(sketch, "E73.trimOffspring", {"start": v(0, 28) * mm, "end": v(-5.77, 23.81) * mm});
            skLineSegment(sketch, "E74.trimOffspring", {"start": v(3.56, 30.6) * mm, "end": v(5.77, 23.81) * mm});
            skLineSegment(sketch, "E75.1.0", {"start": v(-31.22, 15.48) * mm, "end": v(-36, 20.78) * mm});
            skLineSegment(sketch, "E75.1.1", {"start": v(-36, 20.78) * mm, "end": v(-29.02, 19.3) * mm});
            skLineSegment(sketch, "E75.1.2", {"start": v(-29.02, 19.3) * mm, "end": v(-25.46, 25.47) * mm});
            skLineSegment(sketch, "E75.1.3", {"start": v(-25.46, 25.47) * mm, "end": v(-24.71, 18.38) * mm});
            skLineSegment(sketch, "E75.1.4", {"start": v(-24.71, 18.38) * mm, "end": v(-17.74, 16.9) * mm});
            skLineSegment(sketch, "E75.1.5", {"start": v(-17.74, 16.9) * mm, "end": v(-24.25, 14) * mm});
            skLineSegment(sketch, "E75.1.6", {"start": v(-24.25, 14) * mm, "end": v(-23.5, 6.91) * mm});
            skLineSegment(sketch, "E75.1.7", {"start": v(-23.5, 6.91) * mm, "end": v(-28.27, 12.2) * mm});
            skLineSegment(sketch, "E75.1.8", {"start": v(-28.27, 12.2) * mm, "end": v(-34.79, 9.3) * mm});
            skLineSegment(sketch, "E75.1.9", {"start": v(-34.79, 9.3) * mm, "end": v(-31.22, 15.48) * mm});
            skLineSegment(sketch, "E75.2.0", {"start": v(-29.02, -19.3) * mm, "end": v(-36, -20.78) * mm});
            skLineSegment(sketch, "E75.2.1", {"start": v(-36, -20.78) * mm, "end": v(-31.22, -15.48) * mm});
            skLineSegment(sketch, "E75.2.2", {"start": v(-31.22, -15.48) * mm, "end": v(-34.79, -9.3) * mm});
            skLineSegment(sketch, "E75.2.3", {"start": v(-34.79, -9.3) * mm, "end": v(-28.28, -12.2) * mm});
            skLineSegment(sketch, "E75.2.4", {"start": v(-28.28, -12.2) * mm, "end": v(-23.5, -6.91) * mm});
            skLineSegment(sketch, "E75.2.5", {"start": v(-23.5, -6.91) * mm, "end": v(-24.25, -14) * mm});
            skLineSegment(sketch, "E75.2.6", {"start": v(-24.25, -14) * mm, "end": v(-17.74, -16.9) * mm});
            skLineSegment(sketch, "E75.2.7", {"start": v(-17.74, -16.9) * mm, "end": v(-24.71, -18.38) * mm});
            skLineSegment(sketch, "E75.2.8", {"start": v(-24.71, -18.38) * mm, "end": v(-25.46, -25.47) * mm});
            skLineSegment(sketch, "E75.2.9", {"start": v(-25.46, -25.47) * mm, "end": v(-29.02, -19.3) * mm});
            skLineSegment(sketch, "E75.3.0", {"start": v(2.2, -34.78) * mm, "end": v(0, -41.56) * mm});
            skLineSegment(sketch, "E75.3.1", {"start": v(0, -41.56) * mm, "end": v(-2.2, -34.78) * mm});
            skLineSegment(sketch, "E75.3.2", {"start": v(-2.2, -34.78) * mm, "end": v(-9.33, -34.78) * mm});
            skLineSegment(sketch, "E75.3.3", {"start": v(-9.33, -34.78) * mm, "end": v(-3.56, -30.6) * mm});
            skLineSegment(sketch, "E75.3.4", {"start": v(-3.56, -30.6) * mm, "end": v(-5.77, -23.81) * mm});
            skLineSegment(sketch, "E75.3.5", {"start": v(-5.77, -23.81) * mm, "end": v(0, -28) * mm});
            skLineSegment(sketch, "E75.3.6", {"start": v(0, -28) * mm, "end": v(5.77, -23.81) * mm});
            skLineSegment(sketch, "E75.3.7", {"start": v(5.77, -23.81) * mm, "end": v(3.56, -30.6) * mm});
            skLineSegment(sketch, "E75.3.8", {"start": v(3.56, -30.6) * mm, "end": v(9.33, -34.78) * mm});
            skLineSegment(sketch, "E75.3.9", {"start": v(9.33, -34.78) * mm, "end": v(2.2, -34.78) * mm});
            skLineSegment(sketch, "E75.4.0", {"start": v(31.22, -15.48) * mm, "end": v(36, -20.78) * mm});
            skLineSegment(sketch, "E75.4.1", {"start": v(36, -20.78) * mm, "end": v(29.02, -19.3) * mm});
            skLineSegment(sketch, "E75.4.2", {"start": v(29.02, -19.3) * mm, "end": v(25.46, -25.47) * mm});
            skLineSegment(sketch, "E75.4.3", {"start": v(25.46, -25.47) * mm, "end": v(24.71, -18.38) * mm});
            skLineSegment(sketch, "E75.4.4", {"start": v(24.71, -18.38) * mm, "end": v(17.74, -16.9) * mm});
            skLineSegment(sketch, "E75.4.5", {"start": v(17.74, -16.9) * mm, "end": v(24.25, -14) * mm});
            skLineSegment(sketch, "E75.4.6", {"start": v(24.25, -14) * mm, "end": v(23.5, -6.91) * mm});
            skLineSegment(sketch, "E75.4.7", {"start": v(23.5, -6.91) * mm, "end": v(28.27, -12.2) * mm});
            skLineSegment(sketch, "E75.4.8", {"start": v(28.27, -12.2) * mm, "end": v(34.79, -9.3) * mm});
            skLineSegment(sketch, "E75.4.9", {"start": v(34.79, -9.3) * mm, "end": v(31.22, -15.48) * mm});
            skLineSegment(sketch, "E75.5.0", {"start": v(29.02, 19.3) * mm, "end": v(36, 20.78) * mm});
            skLineSegment(sketch, "E75.5.1", {"start": v(36, 20.78) * mm, "end": v(31.22, 15.48) * mm});
            skLineSegment(sketch, "E75.5.2", {"start": v(31.22, 15.48) * mm, "end": v(34.79, 9.3) * mm});
            skLineSegment(sketch, "E75.5.3", {"start": v(34.79, 9.3) * mm, "end": v(28.28, 12.2) * mm});
            skLineSegment(sketch, "E75.5.4", {"start": v(28.28, 12.2) * mm, "end": v(23.5, 6.91) * mm});
            skLineSegment(sketch, "E75.5.5", {"start": v(23.5, 6.91) * mm, "end": v(24.25, 14) * mm});
            skLineSegment(sketch, "E75.5.6", {"start": v(24.25, 14) * mm, "end": v(17.74, 16.9) * mm});
            skLineSegment(sketch, "E75.5.7", {"start": v(17.74, 16.9) * mm, "end": v(24.71, 18.38) * mm});
            skLineSegment(sketch, "E75.5.8", {"start": v(24.71, 18.38) * mm, "end": v(25.46, 25.47) * mm});
            skLineSegment(sketch, "E75.5.9", {"start": v(25.46, 25.47) * mm, "end": v(29.02, 19.3) * mm});
            skPoint(sketch, "E75.center", {"position": v(0, 0) * mm});
            skSolve(sketch);
        }
        {
            var Q0;
            Q0=makeQuery(id+"F6.imprint","IMPRINT",FACE,{"disambiguationData":[TD([[makeQuery(id+"F6.imprint","IMPRINT",EDGE,{"derivedFrom":sQuery(id+"F6.wireOp",EDGE,"E65")}),-1.0]])]});
            var Q1;
            Q1=makeQuery(id+"F6.imprint","IMPRINT",FACE,{"disambiguationData":[TD([[makeQuery(id+"F6.imprint","IMPRINT",EDGE,{"derivedFrom":sQuery(id+"F6.wireOp",EDGE,"E75.5.0")}),-1.0]])]});
            var Q2;
            Q2=makeQuery(id+"F6.imprint","IMPRINT",FACE,{"disambiguationData":[TD([[makeQuery(id+"F6.imprint","IMPRINT",EDGE,{"derivedFrom":sQuery(id+"F6.wireOp",EDGE,"E75.4.0")}),-1.0]])]});
            var Q3;
            Q3=makeQuery(id+"F6.imprint","IMPRINT",FACE,{"disambiguationData":[TD([[makeQuery(id+"F6.imprint","IMPRINT",EDGE,{"derivedFrom":sQuery(id+"F6.wireOp",EDGE,"E75.3.0")}),-1.0]])]});
            var Q4;
            Q4=makeQuery(id+"F6.imprint","IMPRINT",FACE,{"disambiguationData":[TD([[makeQuery(id+"F6.imprint","IMPRINT",EDGE,{"derivedFrom":sQuery(id+"F6.wireOp",EDGE,"E75.1.0")}),-1.0]])]});
            var Q5;
            Q5=makeQuery(id+"F6.imprint","IMPRINT",FACE,{"disambiguationData":[TD([[makeQuery(id+"F6.imprint","IMPRINT",EDGE,{"derivedFrom":sQuery(id+"F6.wireOp",EDGE,"E75.2.0")}),-1.0]])]});
            extrude(context, id + "F7", {"entities" : qUnion([Q0, Q1, Q2, Q3, Q4, Q5]), "operationType" : NewBodyOperationType.REMOVE, "oppositeDirection" : true, "depth" : 25.4 * mm, "offsetDistance" : 25.4 * mm});
        }
        {
            var Q0;
            Q0=makeQuery(id+"F1.opExtrude","CAP_FACE",FACE,{"disambiguationData":[OSD([sQuery(id+"F0.wireOp",EDGE,"E1"),sQuery(id+"F0.wireOp",EDGE,"E2.0"),sQuery(id+"F0.wireOp",EDGE,"E2.1"),sQuery(id+"F0.wireOp",EDGE,"E2.2"),sQuery(id+"F0.wireOp",EDGE,"E2.3"),sQuery(id+"F0.wireOp",EDGE,"E2.4"),sQuery(id+"F0.wireOp",EDGE,"E5.2"),sQuery(id+"F0.wireOp",EDGE,"E5.3"),sQuery(id+"F0.wireOp",EDGE,"E5.4"),sQuery(id+"F0.wireOp",EDGE,"E5.5"),sQuery(id+"F0.wireOp",EDGE,"E6.1.1"),sQuery(id+"F0.wireOp",EDGE,"E6.1.2"),sQuery(id+"F0.wireOp",EDGE,"E3.1.1"),sQuery(id+"F0.wireOp",EDGE,"E6.1.9"),sQuery(id+"F0.wireOp",EDGE,"E3.1.2"),sQuery(id+"F0.wireOp",EDGE,"E3.1.3"),sQuery(id+"F0.wireOp",EDGE,"E3.1.4"),sQuery(id+"F0.wireOp",EDGE,"E3.1.5"),sQuery(id+"F0.wireOp",EDGE,"E3.1.0"),sQuery(id+"F0.wireOp",EDGE,"E6.1.16"),sQuery(id+"F0.wireOp",EDGE,"E6.2.1"),sQuery(id+"F0.wireOp",EDGE,"E6.2.2"),sQuery(id+"F0.wireOp",EDGE,"E3.2.1"),sQuery(id+"F0.wireOp",EDGE,"E6.2.9"),sQuery(id+"F0.wireOp",EDGE,"E3.2.2"),sQuery(id+"F0.wireOp",EDGE,"E3.2.3"),sQuery(id+"F0.wireOp",EDGE,"E3.2.4"),sQuery(id+"F0.wireOp",EDGE,"E3.2.5"),sQuery(id+"F0.wireOp",EDGE,"E3.2.0"),sQuery(id+"F0.wireOp",EDGE,"E6.2.16"),sQuery(id+"F0.wireOp",EDGE,"E6.3.1"),sQuery(id+"F0.wireOp",EDGE,"E6.3.2"),sQuery(id+"F0.wireOp",EDGE,"E4.3.3.0"),sQuery(id+"F0.wireOp",EDGE,"E6.3.9"),sQuery(id+"F0.wireOp",EDGE,"E4.6.3.0"),sQuery(id+"F0.wireOp",EDGE,"E4.9.3.0"),sQuery(id+"F0.wireOp",EDGE,"E4.12.3.0"),sQuery(id+"F0.wireOp",EDGE,"E4.15.3.0"),sQuery(id+"F0.wireOp",EDGE,"E4.2.3.0"),sQuery(id+"F0.wireOp",EDGE,"E6.3.16"),sQuery(id+"F0.wireOp",EDGE,"E6.4.1"),sQuery(id+"F0.wireOp",EDGE,"E6.4.2"),sQuery(id+"F0.wireOp",EDGE,"E4.3.4.0"),sQuery(id+"F0.wireOp",EDGE,"E6.4.9"),sQuery(id+"F0.wireOp",EDGE,"E4.6.4.0"),sQuery(id+"F0.wireOp",EDGE,"E4.9.4.0"),sQuery(id+"F0.wireOp",EDGE,"E4.12.4.0"),sQuery(id+"F0.wireOp",EDGE,"E4.15.4.0"),sQuery(id+"F0.wireOp",EDGE,"E4.2.4.0"),sQuery(id+"F0.wireOp",EDGE,"E6.4.16"),sQuery(id+"F0.wireOp",EDGE,"E6.5.1"),sQuery(id+"F0.wireOp",EDGE,"E6.5.2"),sQuery(id+"F0.wireOp",EDGE,"E2.5"),sQuery(id+"F0.wireOp",EDGE,"E4.3.5.0"),sQuery(id+"F0.wireOp",EDGE,"E6.5.9"),sQuery(id+"F0.wireOp",EDGE,"E4.6.5.0"),sQuery(id+"F0.wireOp",EDGE,"E4.9.5.0"),sQuery(id+"F0.wireOp",EDGE,"E4.12.5.0"),sQuery(id+"F0.wireOp",EDGE,"E4.15.5.0"),sQuery(id+"F0.wireOp",EDGE,"E4.2.5.0"),sQuery(id+"F0.wireOp",EDGE,"E6.5.16"),sQuery(id+"F0.wireOp",EDGE,"E7"),sQuery(id+"F0.wireOp",EDGE,"E8"),sQuery(id+"F0.wireOp",EDGE,"E9"),sQuery(id+"F0.wireOp",EDGE,"E10"),sQuery(id+"F0.wireOp",EDGE,"E11"),sQuery(id+"F0.wireOp",EDGE,"E12")])],"isStart":false});
            var sketch = newSketch(context, id + "F8", { "sketchPlane" : qUnion([Q0])});
            skCircle(sketch, "E76.cCircle", {"center": v(-14.8, 25.63) * mm, "radius": 2.1 * mm, "construction": true});
            skLineSegment(sketch, "E76.0", {"start": v(-12.7, 24.42) * mm, "end": v(-14.8, 23.2) * mm});
            skLineSegment(sketch, "E76.1", {"start": v(-14.8, 23.2) * mm, "end": v(-16.9, 24.42) * mm});
            skLineSegment(sketch, "E76.2", {"start": v(-16.9, 24.42) * mm, "end": v(-16.9, 26.84) * mm});
            skLineSegment(sketch, "E76.3", {"start": v(-16.9, 26.84) * mm, "end": v(-14.8, 28.05) * mm});
            skLineSegment(sketch, "E76.4", {"start": v(-14.8, 28.05) * mm, "end": v(-12.7, 26.84) * mm});
            skLineSegment(sketch, "E76.5", {"start": v(-12.7, 26.84) * mm, "end": v(-12.7, 24.42) * mm});
            skPoint(sketch, "E76.0.midPoint", {"position": v(-13.75, 23.81) * mm});
            skLineSegment(sketch, "E77.1.0", {"start": v(-29.6, 2.42) * mm, "end": v(-27.5, 1.21) * mm});
            skPoint(sketch, "E77.1.1", {"position": v(-27.5, 0) * mm});
            skCircle(sketch, "E77.1.2", {"center": v(-29.6, 0) * mm, "radius": 2.1 * mm, "construction": true});
            skLineSegment(sketch, "E77.1.3", {"start": v(-29.6, -2.42) * mm, "end": v(-31.69, -1.2) * mm});
            skLineSegment(sketch, "E77.1.4", {"start": v(-31.69, -1.2) * mm, "end": v(-31.69, 1.21) * mm});
            skLineSegment(sketch, "E77.1.5", {"start": v(-31.69, 1.21) * mm, "end": v(-29.6, 2.42) * mm});
            skLineSegment(sketch, "E77.1.6", {"start": v(-27.5, -1.21) * mm, "end": v(-29.6, -2.42) * mm});
            skLineSegment(sketch, "E77.1.7", {"start": v(-27.5, 1.21) * mm, "end": v(-27.5, -1.21) * mm});
            skLineSegment(sketch, "E77.2.0", {"start": v(-16.9, -24.42) * mm, "end": v(-14.8, -23.2) * mm});
            skPoint(sketch, "E77.2.1", {"position": v(-13.75, -23.81) * mm});
            skCircle(sketch, "E77.2.2", {"center": v(-14.8, -25.63) * mm, "radius": 2.1 * mm, "construction": true});
            skLineSegment(sketch, "E77.2.3", {"start": v(-12.7, -26.84) * mm, "end": v(-14.8, -28.05) * mm});
            skLineSegment(sketch, "E77.2.4", {"start": v(-14.8, -28.05) * mm, "end": v(-16.9, -26.84) * mm});
            skLineSegment(sketch, "E77.2.5", {"start": v(-16.9, -26.84) * mm, "end": v(-16.9, -24.42) * mm});
            skLineSegment(sketch, "E77.2.6", {"start": v(-12.7, -24.42) * mm, "end": v(-12.7, -26.84) * mm});
            skLineSegment(sketch, "E77.2.7", {"start": v(-14.8, -23.2) * mm, "end": v(-12.7, -24.42) * mm});
            skLineSegment(sketch, "E77.3.0", {"start": v(12.7, -26.84) * mm, "end": v(12.7, -24.42) * mm});
            skPoint(sketch, "E77.3.1", {"position": v(13.75, -23.81) * mm});
            skCircle(sketch, "E77.3.2", {"center": v(14.8, -25.63) * mm, "radius": 2.1 * mm, "construction": true});
            skLineSegment(sketch, "E77.3.3", {"start": v(16.9, -24.42) * mm, "end": v(16.9, -26.84) * mm});
            skLineSegment(sketch, "E77.3.4", {"start": v(16.9, -26.84) * mm, "end": v(14.8, -28.05) * mm});
            skLineSegment(sketch, "E77.3.5", {"start": v(14.8, -28.05) * mm, "end": v(12.7, -26.84) * mm});
            skLineSegment(sketch, "E77.3.6", {"start": v(14.8, -23.2) * mm, "end": v(16.9, -24.42) * mm});
            skLineSegment(sketch, "E77.3.7", {"start": v(12.7, -24.42) * mm, "end": v(14.8, -23.2) * mm});
            skLineSegment(sketch, "E77.4.0", {"start": v(29.6, -2.42) * mm, "end": v(27.5, -1.21) * mm});
            skPoint(sketch, "E77.4.1", {"position": v(27.5, 0) * mm});
            skCircle(sketch, "E77.4.2", {"center": v(29.6, 0) * mm, "radius": 2.1 * mm, "construction": true});
            skLineSegment(sketch, "E77.4.3", {"start": v(29.6, 2.42) * mm, "end": v(31.69, 1.2) * mm});
            skLineSegment(sketch, "E77.4.4", {"start": v(31.69, 1.2) * mm, "end": v(31.69, -1.21) * mm});
            skLineSegment(sketch, "E77.4.5", {"start": v(31.69, -1.21) * mm, "end": v(29.6, -2.42) * mm});
            skLineSegment(sketch, "E77.4.6", {"start": v(27.5, 1.21) * mm, "end": v(29.6, 2.42) * mm});
            skLineSegment(sketch, "E77.4.7", {"start": v(27.5, -1.21) * mm, "end": v(27.5, 1.21) * mm});
            skLineSegment(sketch, "E77.5.0", {"start": v(16.9, 24.42) * mm, "end": v(14.8, 23.2) * mm});
            skPoint(sketch, "E77.5.1", {"position": v(13.75, 23.81) * mm});
            skCircle(sketch, "E77.5.2", {"center": v(14.8, 25.63) * mm, "radius": 2.1 * mm, "construction": true});
            skLineSegment(sketch, "E77.5.3", {"start": v(12.7, 26.84) * mm, "end": v(14.8, 28.05) * mm});
            skLineSegment(sketch, "E77.5.4", {"start": v(14.8, 28.05) * mm, "end": v(16.9, 26.84) * mm});
            skLineSegment(sketch, "E77.5.5", {"start": v(16.9, 26.84) * mm, "end": v(16.9, 24.42) * mm});
            skLineSegment(sketch, "E77.5.6", {"start": v(12.7, 24.42) * mm, "end": v(12.7, 26.84) * mm});
            skLineSegment(sketch, "E77.5.7", {"start": v(14.8, 23.2) * mm, "end": v(12.7, 24.42) * mm});
            skPoint(sketch, "E77.center", {"position": v(0, 0) * mm});
            skSolve(sketch);
        }
        {
            var Q0;
            Q0=makeQuery(id+"F8.imprint","IMPRINT",FACE,{"disambiguationData":[TD([[makeQuery(id+"F8.imprint","IMPRINT",EDGE,{"derivedFrom":sQuery(id+"F8.wireOp",EDGE,"E76.0")}),1.0]])]});
            var Q1;
            Q1=makeQuery(id+"F8.imprint","IMPRINT",FACE,{"disambiguationData":[TD([[makeQuery(id+"F8.imprint","IMPRINT",EDGE,{"derivedFrom":sQuery(id+"F8.wireOp",EDGE,"E77.5.0")}),-1.0]])]});
            var Q2;
            Q2=makeQuery(id+"F8.imprint","IMPRINT",FACE,{"disambiguationData":[TD([[makeQuery(id+"F8.imprint","IMPRINT",EDGE,{"derivedFrom":sQuery(id+"F8.wireOp",EDGE,"E77.4.0")}),-1.0]])]});
            var Q3;
            Q3=makeQuery(id+"F8.imprint","IMPRINT",FACE,{"disambiguationData":[TD([[makeQuery(id+"F8.imprint","IMPRINT",EDGE,{"derivedFrom":sQuery(id+"F8.wireOp",EDGE,"E77.3.0")}),-1.0]])]});
            var Q4;
            Q4=makeQuery(id+"F8.imprint","IMPRINT",FACE,{"disambiguationData":[TD([[makeQuery(id+"F8.imprint","IMPRINT",EDGE,{"derivedFrom":sQuery(id+"F8.wireOp",EDGE,"E77.2.0")}),-1.0]])]});
            var Q5;
            Q5=makeQuery(id+"F8.imprint","IMPRINT",FACE,{"disambiguationData":[TD([[makeQuery(id+"F8.imprint","IMPRINT",EDGE,{"derivedFrom":sQuery(id+"F8.wireOp",EDGE,"E77.1.0")}),-1.0]])]});
            extrude(context, id + "F9", {"entities" : qUnion([Q0, Q1, Q2, Q3, Q4, Q5]), "operationType" : NewBodyOperationType.ADD, "oppositeDirection" : true, "depth" : 6.35 * mm, "offsetDistance" : 25.4 * mm});
        }
    });
